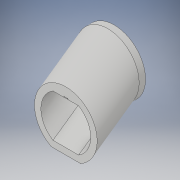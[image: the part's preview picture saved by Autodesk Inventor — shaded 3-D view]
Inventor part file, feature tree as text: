
AUTODESK INVENTOR PART (.ipt)
format: ipt  version: 2017 (Build 210142000, 142)  size: 173,056 bytes
history: native  units: in
note: dims shown in document units (in); Inventor stores cm internally (conversion verified against a paired STEP export)
features: sketch x2, extrude x2, sweep x2, plane x1
ambient origin geometry x8: Origin, YZ Plane, XZ Plane, XY Plane, X Axis, Y Axis, Z Axis, Center Point
bodies: Solid1 (feature_tree), Solid2 (feature_tree), Solid3 (feature_tree)
feature tree (7):
  sketch  "Sketch1"  dims[d0=6.6667in d1=4.0in d2=1.0in d3=1.0in d4=0.0in d12=8.0in]
  extrude  "connecction top"  Depth=1.0in
  extrude  "light flat"  Depth=1.0in
  plane  "Work Plane2"
  sketch  "Sketch6"  dims[d28=8.0in d29=0.3779in d34=0.5833in d35=0.0625in d36=0.0625in d37=0.125in d38=0.25in d39=0.125in d40=45.0deg d41=0.0892in d42=0.0884in d43=1.0in d44=0.0in d45=0.0in d46=0.0in d47=0.0in d48=0.0in]
  sweep  "ramp"
  sweep  "light angle"
